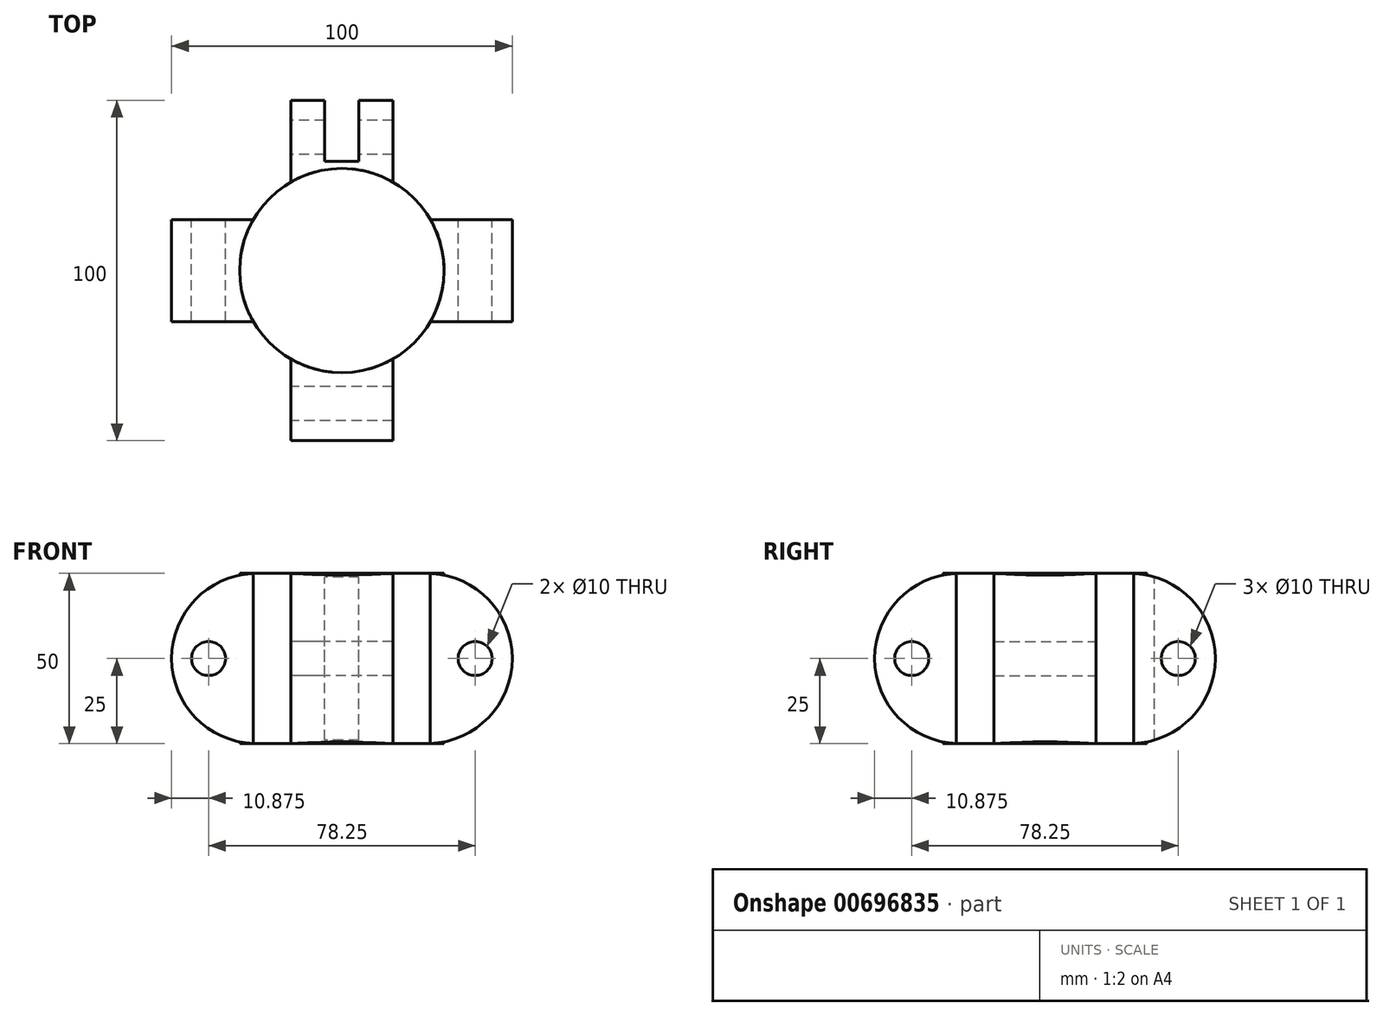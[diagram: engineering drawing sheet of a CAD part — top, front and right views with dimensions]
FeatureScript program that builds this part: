
annotation { "Feature Type Name" : "Feature", "Feature Type Description" : "" }
export const myFeature = defineFeature(function(context is Context, id is Id, definition is map)
    precondition{}
    {
        {
            var Q0;
            Q0=qCreatedBy(makeId("Front.planeOp"),FACE);
            var sketch = newSketch(context, id + "F0", { "sketchPlane" : qUnion([Q0])});
            skLineSegment(sketch, "E0.bottom", {"start": v(0, 0) * mm, "end": v(-25, 0) * mm});
            skLineSegment(sketch, "E0.top", {"start": v(0, 50) * mm, "end": v(-25, 50) * mm});
            skLineSegment(sketch, "E0.left", {"start": v(0, 0) * mm, "end": v(0, 50) * mm});
            skLineSegment(sketch, "E0.right", {"start": v(-25, 0) * mm, "end": v(-25, 50) * mm});
            skArc(sketch, "E1", {"start": v(-25, 50) * mm, "mid": v(-50, 25) * mm, "end": v(-25, 0) * mm});
            skCircle(sketch, "E2", {"center": v(-39.12, 25) * mm, "radius": 5 * mm});
            skLineSegment(sketch, "E3", {"start": v(0, -43.63) * mm, "end": v(0, 64.87) * mm, "construction": true});
            skArc(sketch, "E4.MirrorCS", {"start": v(25, 50) * mm, "mid": v(50, 25) * mm, "end": v(25, 0) * mm});
            skCircle(sketch, "E5.MirrorC", {"center": v(39.12, 25) * mm, "radius": 5 * mm});
            skLineSegment(sketch, "E6.MirrorCS", {"start": v(25, 0) * mm, "end": v(25, 50) * mm});
            skLineSegment(sketch, "E7.MirrorCS", {"start": v(0, 50) * mm, "end": v(25, 50) * mm});
            skLineSegment(sketch, "E8.MirrorCS", {"start": v(0, 0) * mm, "end": v(25, 0) * mm});
            skSolve(sketch);
        }
        {
            var Q0;
            Q0 = qSketchRegion(id + "F0", true);
            extrude(context, id + "F1", {"entities" : qUnion([Q0]), "depth" : 15 * mm, "offsetDistance" : 25 * mm, "hasSecondDirection" : true, "secondDirectionOppositeDirection" : true, "secondDirectionDepth" : 15 * mm});
        }
        {
            var Q0;
            Q0=makeQuery(id+"F1.opExtrude","SWEPT_BODY",BODY,{"disambiguationData":[OSD([sQuery(id+"F0.wireOp",EDGE,"E0.bottom"),sQuery(id+"F0.wireOp",EDGE,"E0.top"),sQuery(id+"F0.wireOp",EDGE,"E1"),sQuery(id+"F0.wireOp",EDGE,"E2"),sQuery(id+"F0.wireOp",EDGE,"E4.MirrorCS"),sQuery(id+"F0.wireOp",EDGE,"E5.MirrorC"),sQuery(id+"F0.wireOp",EDGE,"E7.MirrorCS"),sQuery(id+"F0.wireOp",EDGE,"E8.MirrorCS")])]});
            var Q1;
            Q1=sQuery(id+"F0.wireOp",EDGE,"E3");
            circularPattern(context, id + "F2", {"operationType" : NewBodyOperationType.ADD, "entities" : qUnion([Q0]), "axis" : qUnion([Q1]), "angle" : 90 * degree, "instanceCount" : 2, "equalSpace" : true});
        }
        {
            var Q0;
            Q0=makeQuery(id+"F2.opPattern","COPY",FACE,{"derivedFrom":makeQuery(id+"F1.opExtrude","SWEPT_FACE",FACE,{"disambiguationData":[OSD([sQuery(id+"F0.wireOp",EDGE,"E0.top"),sQuery(id+"F0.wireOp",EDGE,"E7.MirrorCS")])]}),"instanceName":"1"});
            var sketch = newSketch(context, id + "F3", { "sketchPlane" : qUnion([Q0])});
            skCircle(sketch, "E9", {"center": v(0, 0) * mm, "radius": 30 * mm});
            skSolve(sketch);
        }
        {
            var Q0;
            Q0 = qSketchRegion(id + "F3", true);
            var Q1;
            Q1=makeQuery(id+"F2.opPattern","COPY",FACE,{"derivedFrom":makeQuery(id+"F1.opExtrude","SWEPT_FACE",FACE,{"disambiguationData":[OSD([sQuery(id+"F0.wireOp",EDGE,"E0.bottom"),sQuery(id+"F0.wireOp",EDGE,"E8.MirrorCS")])]}),"instanceName":"1"});
            extrude(context, id + "F4", {"entities" : qUnion([Q0]), "operationType" : NewBodyOperationType.ADD, "endBound" : BoundingType.UP_TO_SURFACE, "oppositeDirection" : true, "depth" : 25 * mm, "endBoundEntityFace" : qUnion([Q1]), "offsetDistance" : 25 * mm});
        }
        {
            var Q0;
            {var subQ0=makeQuery(id+"F1.opExtrude","SWEPT_FACE",FACE,{"disambiguationData":[OSD([sQuery(id+"F0.wireOp",EDGE,"E0.top"),sQuery(id+"F0.wireOp",EDGE,"E7.MirrorCS")])]});Q0=makeQuery(id+"F4.boolean.opBoolean","MERGE",FACE,{"derivedFrom":[makeQuery(id+"F2.boolean.opBoolean","MERGE",FACE,{"derivedFrom":[subQ0,makeQuery(id+"F2.opPattern","COPY",FACE,{"derivedFrom":subQ0,"instanceName":"1"})]}),makeQuery(id+"F4.opExtrude","CAP_FACE",FACE,{"disambiguationData":[OSD([sQuery(id+"F3.wireOp",EDGE,"E9")])],"isStart":true})]});}
            var sketch = newSketch(context, id + "F5", { "sketchPlane" : qUnion([Q0])});
            skLineSegment(sketch, "E10.bottom", {"start": v(5, 32.12) * mm, "end": v(-5, 32.12) * mm});
            skLineSegment(sketch, "E10.top", {"start": v(5, 96.13) * mm, "end": v(-5, 96.13) * mm});
            skLineSegment(sketch, "E10.left", {"start": v(5, 32.12) * mm, "end": v(5, 96.13) * mm});
            skLineSegment(sketch, "E10.right", {"start": v(-5, 32.12) * mm, "end": v(-5, 96.13) * mm});
            skPoint(sketch, "E10.middle", {"position": v(0, 64.13) * mm});
            skLineSegment(sketch, "E11.bottom", {"start": v(0, 32.12) * mm, "end": v(0, 32.12) * mm});
            skLineSegment(sketch, "E11.top", {"start": v(0, 32.12) * mm, "end": v(0, 32.12) * mm});
            skLineSegment(sketch, "E11.left", {"start": v(0, 32.12) * mm, "end": v(0, 32.12) * mm});
            skLineSegment(sketch, "E11.right", {"start": v(0, 32.12) * mm, "end": v(0, 32.12) * mm});
            skPoint(sketch, "E11.middle", {"position": v(0, 32.12) * mm});
            skPoint(sketch, "E11.cornerSnap0", {"position": v(0, 32.12) * mm});
            skSolve(sketch);
        }
        {
            var Q0;
            Q0=makeQuery(id+"F5.imprint","IMPRINT",FACE,{"disambiguationData":[TD([[makeQuery(id+"F5.imprint","IMPRINT",EDGE,{"derivedFrom":sQuery(id+"F5.wireOp",EDGE,"E10.top")}),1.0]])]});
            extrude(context, id + "F6", {"entities" : qUnion([Q0]), "operationType" : NewBodyOperationType.REMOVE, "endBound" : BoundingType.THROUGH_ALL, "oppositeDirection" : true, "depth" : 25 * mm, "offsetDistance" : 25 * mm});
        }
    });
